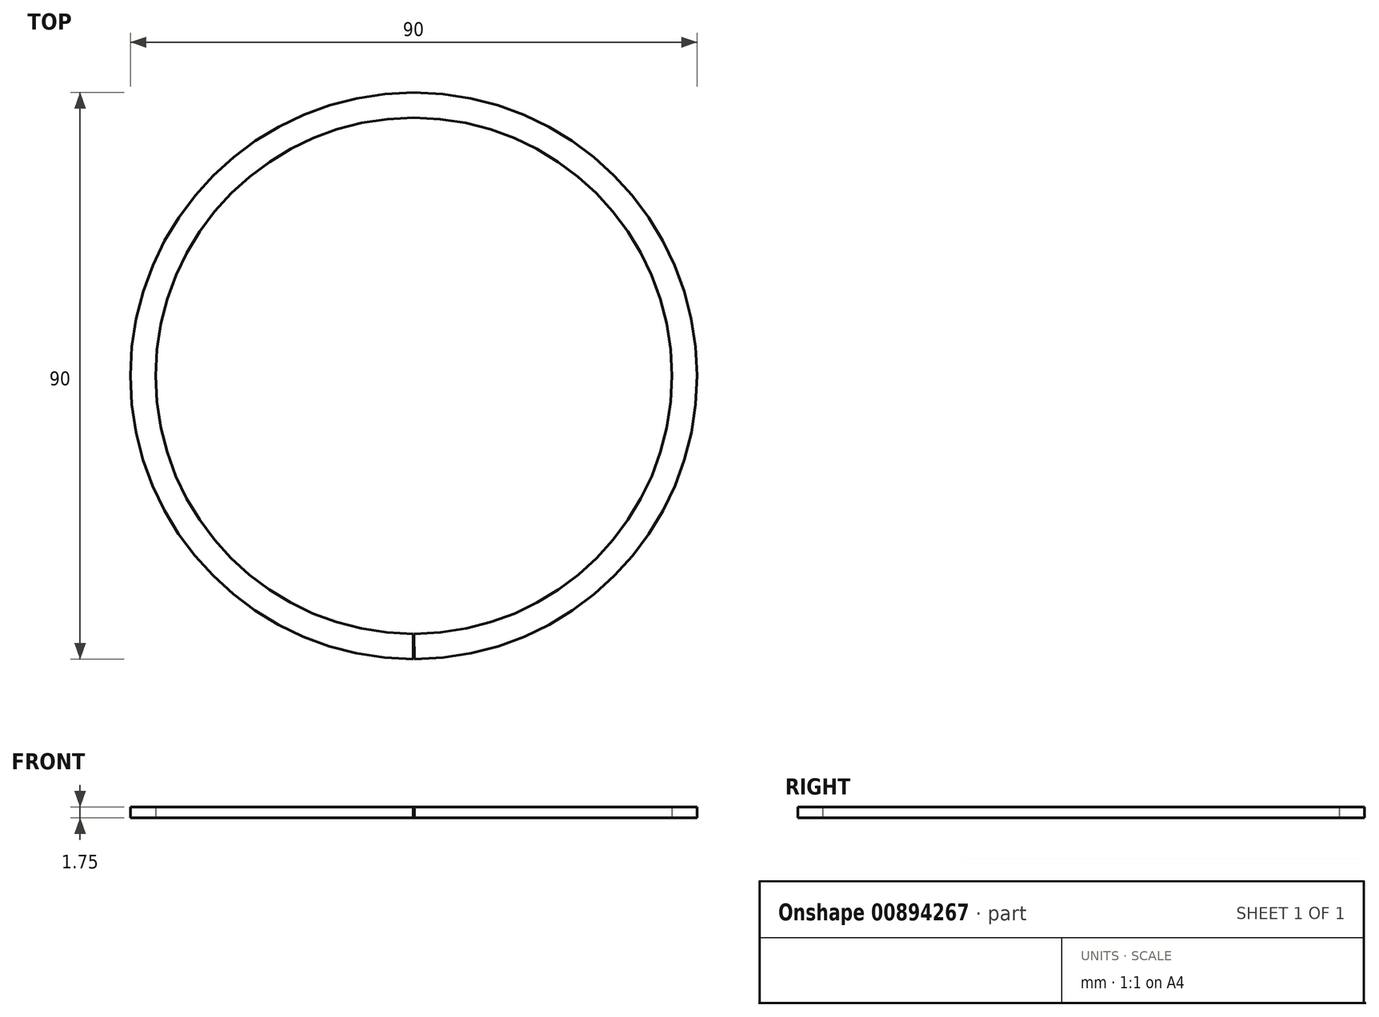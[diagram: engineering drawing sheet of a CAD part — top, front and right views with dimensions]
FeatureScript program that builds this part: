
annotation { "Feature Type Name" : "Feature", "Feature Type Description" : "" }
export const myFeature = defineFeature(function(context is Context, id is Id, definition is map)
    precondition{}
    {
        {
            var Q0;
            Q0=qCreatedBy(makeId("Right.planeOp"),FACE);
            var sketch = newSketch(context, id + "F0", { "sketchPlane" : qUnion([Q0])});
            skLineSegment(sketch, "E0.bottom", {"start": v(41, 0) * mm, "end": v(45, 0) * mm});
            skLineSegment(sketch, "E0.top", {"start": v(41, 1.75) * mm, "end": v(45, 1.75) * mm});
            skLineSegment(sketch, "E0.left", {"start": v(41, 0) * mm, "end": v(41, 1.75) * mm});
            skLineSegment(sketch, "E0.right", {"start": v(45, 0) * mm, "end": v(45, 1.75) * mm});
            skLineSegment(sketch, "E1", {"start": v(0, 0) * mm, "end": v(41, 0) * mm, "construction": true});
            skLineSegment(sketch, "E2", {"start": v(0, 0) * mm, "end": v(0, 20) * mm, "construction": true});
            skSolve(sketch);
        }
        {
            var Q0;
            Q0=makeQuery(id+"F0.imprint","IMPRINT",FACE,{"disambiguationData":[TD([[makeQuery(id+"F0.imprint","IMPRINT",EDGE,{"derivedFrom":sQuery(id+"F0.wireOp",EDGE,"E0.bottom")}),1.0]])]});
            var Q1;
            Q1=sQuery(id+"F0.wireOp",EDGE,"E2");
            revolve(context, id + "F1", {"surfaceOperationType" : NewSurfaceOperationType.NEW, "entities" : qUnion([Q0]), "axis" : qUnion([Q1]), "revolveType" : RevolveType.TWO_DIRECTIONS, "angle" : 179.9 * degree, "angleBack" : 180.1 * degree});
        }
    });
